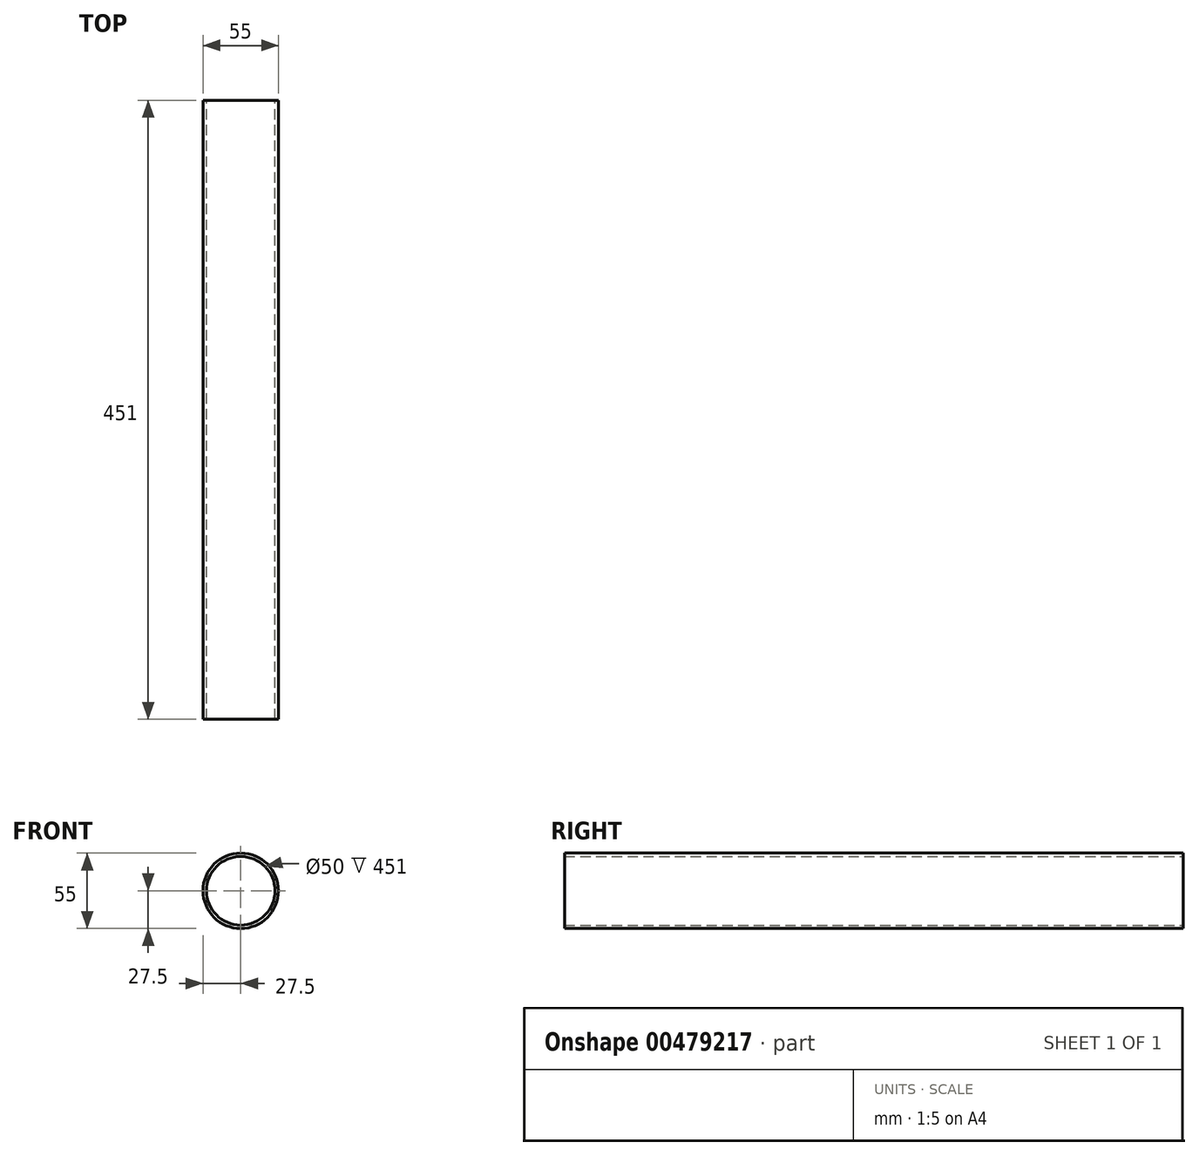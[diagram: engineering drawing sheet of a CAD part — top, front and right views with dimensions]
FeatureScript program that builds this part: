
annotation { "Feature Type Name" : "Feature", "Feature Type Description" : "" }
export const myFeature = defineFeature(function(context is Context, id is Id, definition is map)
    precondition{}
    {
        {
            var Q0;
            Q0=qCreatedBy(makeId("Front.planeOp"),FACE);
            var sketch = newSketch(context, id + "F0", { "sketchPlane" : qUnion([Q0])});
            skCircle(sketch, "E0", {"center": v(0, 0) * mm, "radius": 27.5 * mm});
            skCircle(sketch, "E1", {"center": v(0, 0) * mm, "radius": 25 * mm});
            skSolve(sketch);
        }
        {
            var Q0;
            Q0=makeQuery(id+"F0.imprint","IMPRINT",FACE,{"disambiguationData":[TD([[makeQuery(id+"F0.imprint","IMPRINT",EDGE,{"derivedFrom":sQuery(id+"F0.wireOp",EDGE,"E0")}),1.0]])]});
            extrude(context, id + "F1", {"entities" : qUnion([Q0]), "depth" : 451 * mm});
        }
    });
